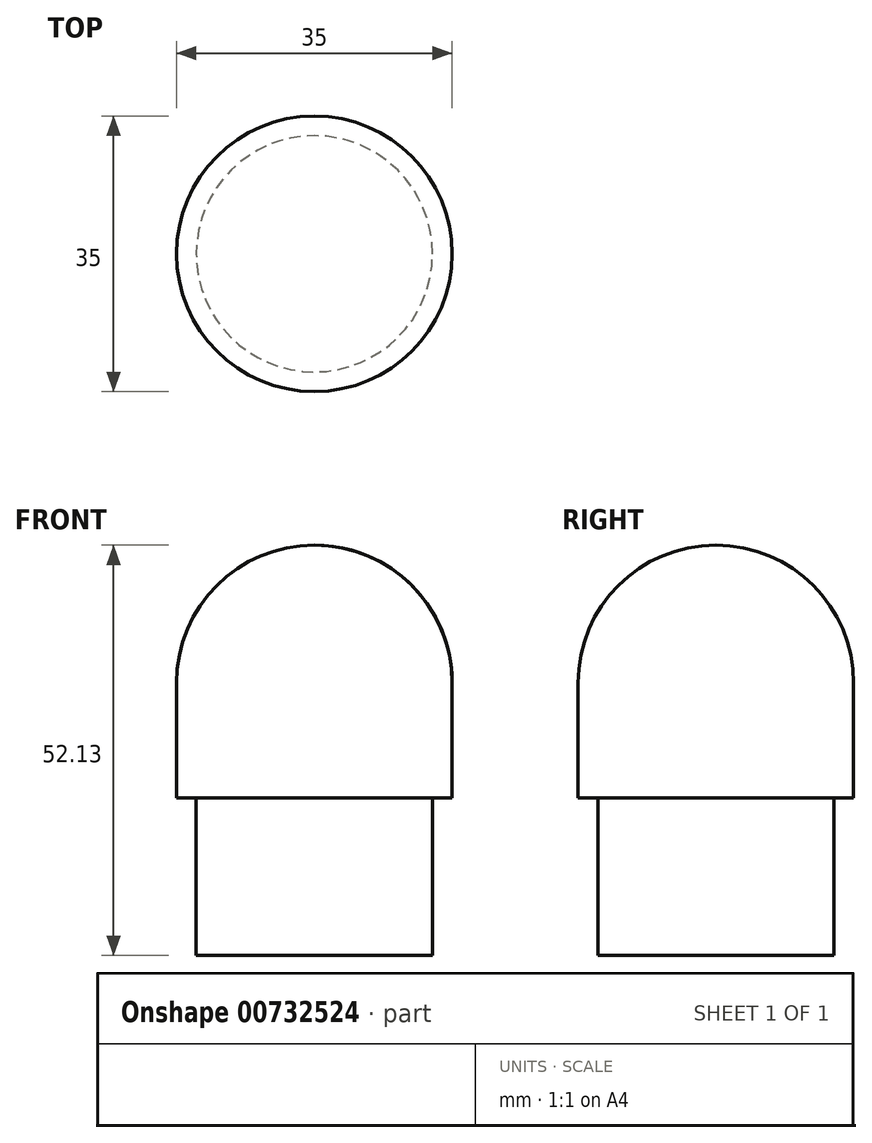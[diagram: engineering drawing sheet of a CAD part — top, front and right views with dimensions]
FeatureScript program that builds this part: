
annotation { "Feature Type Name" : "Feature", "Feature Type Description" : "" }
export const myFeature = defineFeature(function(context is Context, id is Id, definition is map)
    precondition{}
    {
        {
            var Q0;
            Q0=qCreatedBy(makeId("Front.planeOp"),FACE);
            var sketch = newSketch(context, id + "F0", { "sketchPlane" : qUnion([Q0])});
            skLineSegment(sketch, "E0", {"start": v(0, -38.63) * mm, "end": v(15, -38.63) * mm});
            skLineSegment(sketch, "E1", {"start": v(15, -38.63) * mm, "end": v(15, -18.63) * mm});
            skLineSegment(sketch, "E2", {"start": v(15, -18.63) * mm, "end": v(17.5, -18.63) * mm});
            skLineSegment(sketch, "E3", {"start": v(17.5, -18.63) * mm, "end": v(17.5, -4) * mm});
            skArc(sketch, "E4", {"start": v(17.5, -4) * mm, "mid": v(12.37, 8.38) * mm, "end": v(0, 13.5) * mm});
            skLineSegment(sketch, "E5", {"start": v(0, 13.5) * mm, "end": v(0, -38.63) * mm});
            skSolve(sketch);
        }
        {
            var Q0;
            Q0=makeQuery(id+"F0.imprint","IMPRINT",FACE,{"disambiguationData":[TD([[makeQuery(id+"F0.imprint","IMPRINT",EDGE,{"derivedFrom":sQuery(id+"F0.wireOp",EDGE,"E0")}),1.0]])]});
            var Q1;
            Q1=sQuery(id+"F0.wireOp",EDGE,"E5");
            revolve(context, id + "F1", {"surfaceOperationType" : NewSurfaceOperationType.NEW, "entities" : qUnion([Q0]), "axis" : qUnion([Q1]), "revolveType" : RevolveType.FULL});
        }
    });
